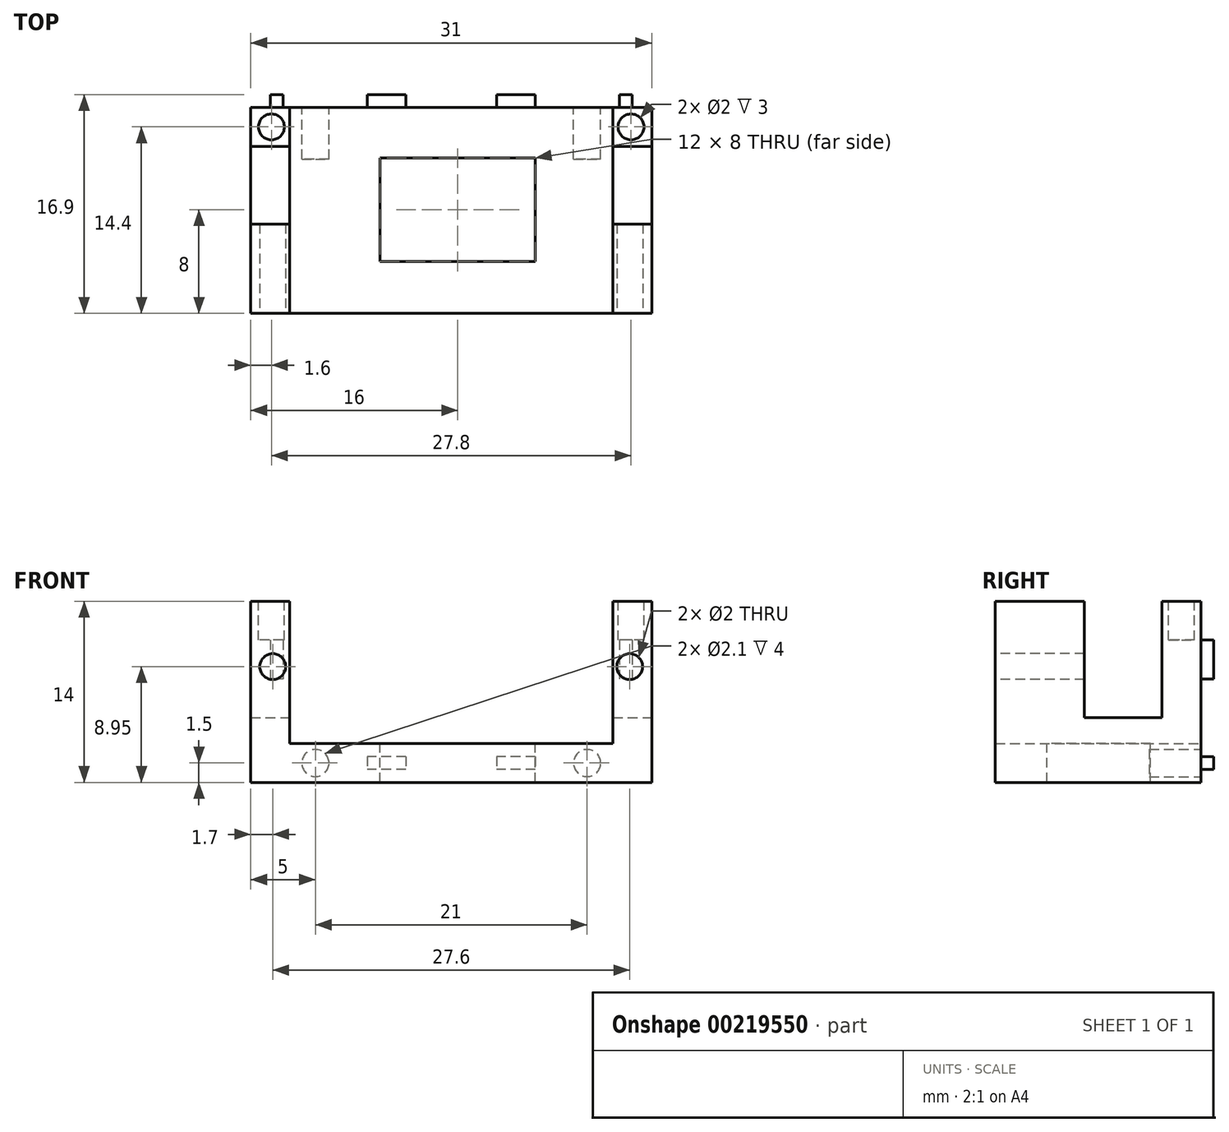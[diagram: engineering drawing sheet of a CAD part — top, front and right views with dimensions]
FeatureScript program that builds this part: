
annotation { "Feature Type Name" : "Feature", "Feature Type Description" : "" }
export const myFeature = defineFeature(function(context is Context, id is Id, definition is map)
    precondition{}
    {
        {
            var Q0;
            Q0=qCreatedBy(makeId("Front.planeOp"),FACE);
            var sketch = newSketch(context, id + "F0", { "sketchPlane" : qUnion([Q0])});
            skLineSegment(sketch, "E0.bottom", {"start": v(0, 14) * mm, "end": v(3, 14) * mm});
            skLineSegment(sketch, "E0.top", {"start": v(0, 3) * mm, "end": v(3, 3) * mm});
            skLineSegment(sketch, "E0.left", {"start": v(0, 14) * mm, "end": v(0, 3) * mm});
            skLineSegment(sketch, "E0.right", {"start": v(3, 14) * mm, "end": v(3, 3) * mm});
            skLineSegment(sketch, "E1.bottom", {"start": v(28, 14) * mm, "end": v(31, 14) * mm});
            skLineSegment(sketch, "E1.top", {"start": v(28, 3) * mm, "end": v(31, 3) * mm});
            skLineSegment(sketch, "E1.left", {"start": v(28, 14) * mm, "end": v(28, 3) * mm});
            skLineSegment(sketch, "E1.right", {"start": v(31, 14) * mm, "end": v(31, 3) * mm});
            skLineSegment(sketch, "E2.bottom", {"start": v(0, 3) * mm, "end": v(31, 3) * mm});
            skLineSegment(sketch, "E2.top", {"start": v(0, 0) * mm, "end": v(31, 0) * mm});
            skLineSegment(sketch, "E2.left", {"start": v(0, 3) * mm, "end": v(0, 0) * mm});
            skLineSegment(sketch, "E2.right", {"start": v(31, 3) * mm, "end": v(31, 0) * mm});
            skSolve(sketch);
        }
        {
            var Q0;
            Q0 = qSketchRegion(id + "F0", true);
            extrude(context, id + "F1", {"entities" : qUnion([Q0]), "depth" : 15.9 * mm});
        }
        {
            var Q0;
            Q0=makeQuery(id+"F1.opExtrude","SWEPT_FACE",FACE,{"disambiguationData":[OSD([sQuery(id+"F0.wireOp",EDGE,"E1.right"),sQuery(id+"F0.wireOp",EDGE,"E2.right")])]});
            var sketch = newSketch(context, id + "F2", { "sketchPlane" : qUnion([Q0])});
            skLineSegment(sketch, "E3.bottom", {"start": v(-3, 14) * mm, "end": v(-9, 14) * mm});
            skLineSegment(sketch, "E3.top", {"start": v(-3, 5) * mm, "end": v(-9, 5) * mm});
            skLineSegment(sketch, "E3.left", {"start": v(-3, 14) * mm, "end": v(-3, 5) * mm});
            skLineSegment(sketch, "E3.right", {"start": v(-9, 14) * mm, "end": v(-9, 5) * mm});
            skSolve(sketch);
        }
        {
            var Q0;
            Q0 = qSketchRegion(id + "F2", true);
            extrude(context, id + "F3", {"entities" : qUnion([Q0]), "operationType" : NewBodyOperationType.REMOVE, "endBound" : BoundingType.THROUGH_ALL, "oppositeDirection" : true, "depth" : 25 * mm});
        }
        {
            var Q0;
            Q0=makeQuery(id+"F1.opExtrude","CAP_FACE",FACE,{"disambiguationData":[OSD([sQuery(id+"F0.wireOp",EDGE,"E0.bottom"),sQuery(id+"F0.wireOp",EDGE,"E0.left"),sQuery(id+"F0.wireOp",EDGE,"E0.right"),sQuery(id+"F0.wireOp",EDGE,"E1.bottom"),sQuery(id+"F0.wireOp",EDGE,"E1.left"),sQuery(id+"F0.wireOp",EDGE,"E1.right"),sQuery(id+"F0.wireOp",EDGE,"E2.bottom"),sQuery(id+"F0.wireOp",EDGE,"E2.top"),sQuery(id+"F0.wireOp",EDGE,"E2.left"),sQuery(id+"F0.wireOp",EDGE,"E2.right")])],"isStart":false});
            var sketch = newSketch(context, id + "F4", { "sketchPlane" : qUnion([Q0])});
            skCircle(sketch, "E4", {"center": v(1.7, 8.95) * mm, "radius": 1 * mm});
            skCircle(sketch, "E5", {"center": v(29.3, 8.95) * mm, "radius": 1 * mm});
            skSolve(sketch);
        }
        {
            var Q0;
            Q0 = qSketchRegion(id + "F4", true);
            var Q1;
            Q1=makeQuery(id+"F3.boolean.opBoolean","COPY",FACE,{"disambiguationData":[TD([makeQuery(id+"F1.opExtrude","SWEPT_FACE",FACE,{"disambiguationData":[OSD([sQuery(id+"F0.wireOp",EDGE,"E0.right")])]})])],"derivedFrom":makeQuery(id+"F3.opExtrude","SWEPT_FACE",FACE,{"disambiguationData":[OSD([sQuery(id+"F2.wireOp",EDGE,"E3.right")])]})});
            extrude(context, id + "F5", {"entities" : qUnion([Q0]), "operationType" : NewBodyOperationType.REMOVE, "endBound" : BoundingType.UP_TO_SURFACE, "oppositeDirection" : true, "endBoundEntityFace" : qUnion([Q1]), "depth" : 25 * mm});
        }
        {
            var Q0;
            Q0=makeQuery(id+"F1.opExtrude","CAP_FACE",FACE,{"disambiguationData":[OSD([sQuery(id+"F0.wireOp",EDGE,"E0.bottom"),sQuery(id+"F0.wireOp",EDGE,"E0.left"),sQuery(id+"F0.wireOp",EDGE,"E0.right"),sQuery(id+"F0.wireOp",EDGE,"E1.bottom"),sQuery(id+"F0.wireOp",EDGE,"E1.left"),sQuery(id+"F0.wireOp",EDGE,"E1.right"),sQuery(id+"F0.wireOp",EDGE,"E2.bottom"),sQuery(id+"F0.wireOp",EDGE,"E2.top"),sQuery(id+"F0.wireOp",EDGE,"E2.left"),sQuery(id+"F0.wireOp",EDGE,"E2.right")])],"isStart":true});
            var sketch = newSketch(context, id + "F6", { "sketchPlane" : qUnion([Q0])});
            skCircle(sketch, "E6", {"center": v(-26, 1.5) * mm, "radius": 1.05 * mm});
            skCircle(sketch, "E7", {"center": v(-5, 1.5) * mm, "radius": 1.05 * mm});
            skSolve(sketch);
        }
        {
            var Q0;
            Q0 = qSketchRegion(id + "F6", true);
            extrude(context, id + "F7", {"entities" : qUnion([Q0]), "operationType" : NewBodyOperationType.REMOVE, "oppositeDirection" : true, "depth" : 4 * mm});
        }
        {
            var Q0;
            Q0=makeQuery(id+"F1.opExtrude","CAP_FACE",FACE,{"disambiguationData":[OSD([sQuery(id+"F0.wireOp",EDGE,"E0.bottom"),sQuery(id+"F0.wireOp",EDGE,"E0.left"),sQuery(id+"F0.wireOp",EDGE,"E0.right"),sQuery(id+"F0.wireOp",EDGE,"E1.bottom"),sQuery(id+"F0.wireOp",EDGE,"E1.left"),sQuery(id+"F0.wireOp",EDGE,"E1.right"),sQuery(id+"F0.wireOp",EDGE,"E2.bottom"),sQuery(id+"F0.wireOp",EDGE,"E2.top"),sQuery(id+"F0.wireOp",EDGE,"E2.left"),sQuery(id+"F0.wireOp",EDGE,"E2.right")])],"isStart":true});
            var sketch = newSketch(context, id + "F8", { "sketchPlane" : qUnion([Q0])});
            skLineSegment(sketch, "E8.bottom", {"start": v(-22, 2) * mm, "end": v(-19, 2) * mm});
            skLineSegment(sketch, "E8.top", {"start": v(-22, 1) * mm, "end": v(-19, 1) * mm});
            skLineSegment(sketch, "E8.left", {"start": v(-22, 2) * mm, "end": v(-22, 1) * mm});
            skLineSegment(sketch, "E8.right", {"start": v(-19, 2) * mm, "end": v(-19, 1) * mm});
            skLineSegment(sketch, "E9.bottom", {"start": v(-12, 2) * mm, "end": v(-9, 2) * mm});
            skLineSegment(sketch, "E9.top", {"start": v(-12, 1) * mm, "end": v(-9, 1) * mm});
            skLineSegment(sketch, "E9.left", {"start": v(-12, 2) * mm, "end": v(-12, 1) * mm});
            skLineSegment(sketch, "E9.right", {"start": v(-9, 2) * mm, "end": v(-9, 1) * mm});
            skLineSegment(sketch, "E10.bottom", {"start": v(-29.5, 11) * mm, "end": v(-28.5, 11) * mm});
            skLineSegment(sketch, "E10.top", {"start": v(-29.5, 8) * mm, "end": v(-28.5, 8) * mm});
            skLineSegment(sketch, "E10.left", {"start": v(-29.5, 11) * mm, "end": v(-29.5, 8) * mm});
            skLineSegment(sketch, "E10.right", {"start": v(-28.5, 11) * mm, "end": v(-28.5, 8) * mm});
            skLineSegment(sketch, "E11.bottom", {"start": v(-2.5, 11) * mm, "end": v(-1.5, 11) * mm});
            skLineSegment(sketch, "E11.top", {"start": v(-2.5, 8) * mm, "end": v(-1.5, 8) * mm});
            skLineSegment(sketch, "E11.left", {"start": v(-2.5, 11) * mm, "end": v(-2.5, 8) * mm});
            skLineSegment(sketch, "E11.right", {"start": v(-1.5, 11) * mm, "end": v(-1.5, 8) * mm});
            skSolve(sketch);
        }
        {
            var Q0;
            Q0 = qSketchRegion(id + "F8", true);
            extrude(context, id + "F9", {"entities" : qUnion([Q0]), "operationType" : NewBodyOperationType.ADD, "depth" : 1 * mm});
        }
        {
            var Q0;
            Q0=makeQuery(id+"F1.opExtrude","SWEPT_FACE",FACE,{"disambiguationData":[OSD([sQuery(id+"F0.wireOp",EDGE,"E1.bottom")])]});
            var sketch = newSketch(context, id + "F10", { "sketchPlane" : qUnion([Q0])});
            skCircle(sketch, "E12", {"center": v(29.4, -1.5) * mm, "radius": 1 * mm});
            skCircle(sketch, "E13", {"center": v(1.6, -1.5) * mm, "radius": 1 * mm});
            skSolve(sketch);
        }
        {
            var Q0;
            Q0 = qSketchRegion(id + "F10", true);
            extrude(context, id + "F11", {"entities" : qUnion([Q0]), "operationType" : NewBodyOperationType.REMOVE, "oppositeDirection" : true, "depth" : 3 * mm});
        }
        {
            var Q0;
            Q0=makeQuery(id+"F3.boolean.opBoolean","MERGE",FACE,{"derivedFrom":[makeQuery(id+"F1.opExtrude","SWEPT_FACE",FACE,{"disambiguationData":[OSD([sQuery(id+"F0.wireOp",EDGE,"E2.bottom")])]}),makeQuery(id+"F3.opExtrude","SWEPT_FACE",FACE,{"disambiguationData":[OSD([sQuery(id+"F2.wireOp",EDGE,"E3.top")])]})]});
            var sketch = newSketch(context, id + "F12", { "sketchPlane" : qUnion([Q0])});
            skLineSegment(sketch, "E14.bottom", {"start": v(10, -3.9) * mm, "end": v(22, -3.9) * mm});
            skLineSegment(sketch, "E14.top", {"start": v(10, -11.9) * mm, "end": v(22, -11.9) * mm});
            skLineSegment(sketch, "E14.left", {"start": v(10, -3.9) * mm, "end": v(10, -11.9) * mm});
            skLineSegment(sketch, "E14.right", {"start": v(22, -3.9) * mm, "end": v(22, -11.9) * mm});
            skSolve(sketch);
        }
        {
            var Q0;
            Q0 = qSketchRegion(id + "F12", true);
            var Q1;
            Q1=makeQuery(id+"F1.opExtrude","SWEPT_FACE",FACE,{"disambiguationData":[OSD([sQuery(id+"F0.wireOp",EDGE,"E2.top")])]});
            extrude(context, id + "F13", {"entities" : qUnion([Q0]), "operationType" : NewBodyOperationType.REMOVE, "endBound" : BoundingType.UP_TO_SURFACE, "oppositeDirection" : true, "endBoundEntityFace" : qUnion([Q1]), "depth" : 25 * mm});
        }
    });
